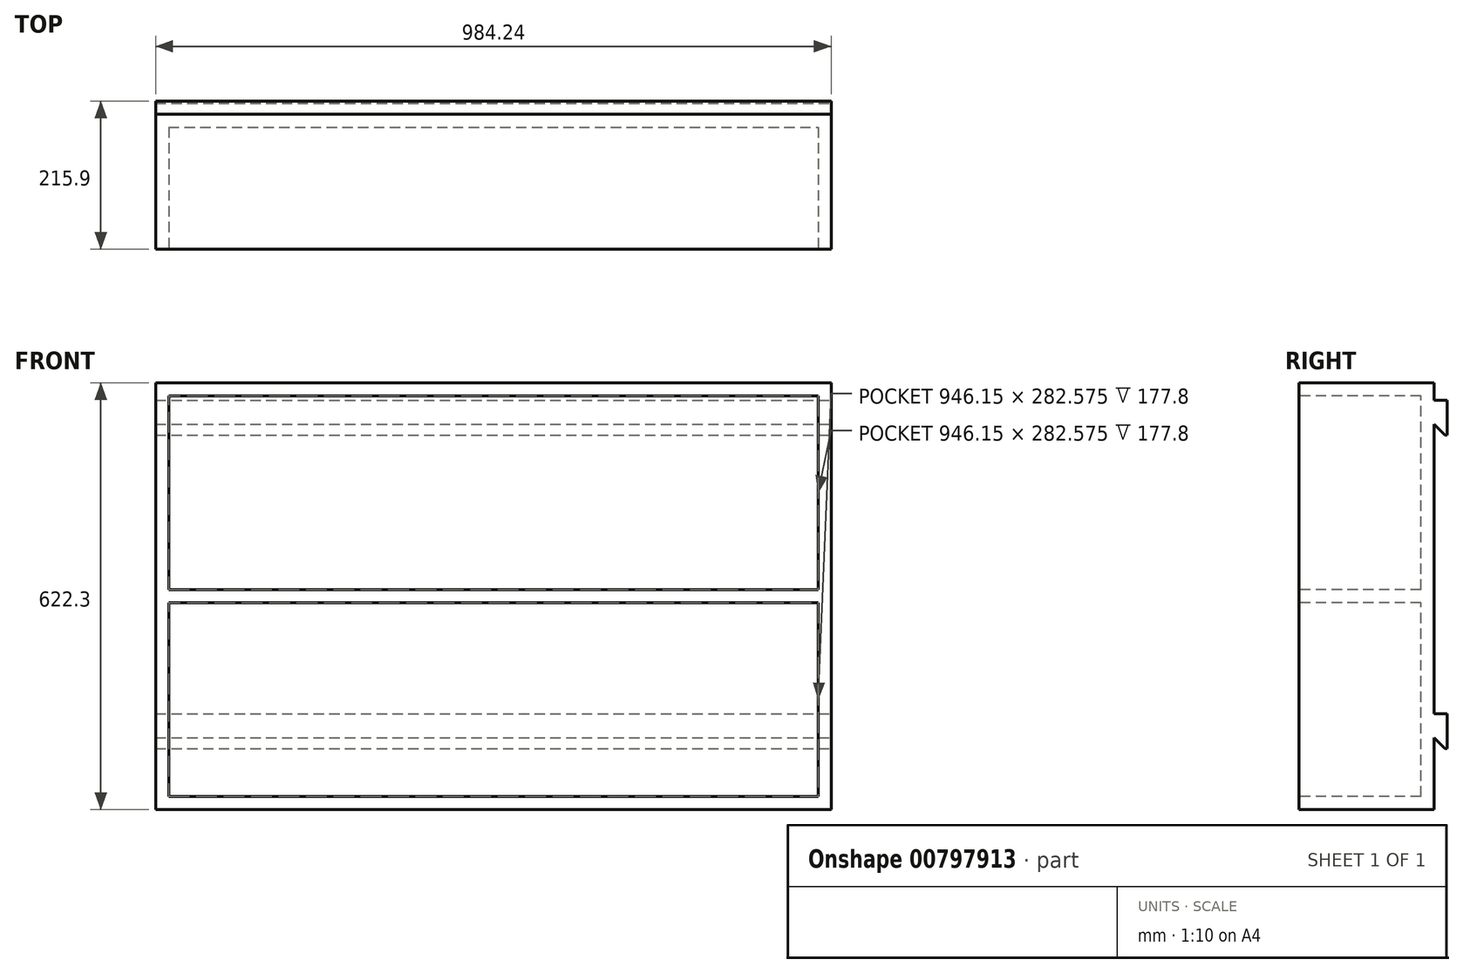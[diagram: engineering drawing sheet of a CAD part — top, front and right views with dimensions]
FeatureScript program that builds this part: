
annotation { "Feature Type Name" : "Feature", "Feature Type Description" : "" }
export const myFeature = defineFeature(function(context is Context, id is Id, definition is map)
    precondition{}
    {
        {
            var Q0;
            Q0=qCreatedBy(makeId("Front.planeOp"),FACE);
            var sketch = newSketch(context, id + "F0", { "sketchPlane" : qUnion([Q0])});
            skLineSegment(sketch, "E0.bottom", {"start": v(-492.12, -311.15) * mm, "end": v(492.13, -311.15) * mm});
            skLineSegment(sketch, "E0.top", {"start": v(-492.13, 311.15) * mm, "end": v(492.12, 311.15) * mm});
            skLineSegment(sketch, "E0.left", {"start": v(-492.12, -311.15) * mm, "end": v(-492.13, 311.15) * mm});
            skLineSegment(sketch, "E0.right", {"start": v(492.13, -311.15) * mm, "end": v(492.12, 311.15) * mm});
            skPoint(sketch, "E0.middle", {"position": v(0, 0) * mm});
            skLineSegment(sketch, "E1.0", {"start": v(-473.07, -292.1) * mm, "end": v(-473.08, 292.1) * mm});
            skLineSegment(sketch, "E1.1", {"start": v(-473.07, -292.1) * mm, "end": v(473.08, -292.1) * mm});
            skLineSegment(sketch, "E1.2", {"start": v(473.08, -292.1) * mm, "end": v(473.07, 292.1) * mm});
            skLineSegment(sketch, "E1.3", {"start": v(-473.08, 292.1) * mm, "end": v(473.07, 292.1) * mm});
            skLineSegment(sketch, "E2.0", {"start": v(-473.07, -9.53) * mm, "end": v(473.07, -9.53) * mm});
            skLineSegment(sketch, "E3.0", {"start": v(-473.07, 9.52) * mm, "end": v(473.07, 9.52) * mm});
            skSolve(sketch);
        }
        {
            var Q0;
            Q0=makeQuery(id+"F0.imprint","IMPRINT",FACE,{"disambiguationData":[TD([[makeQuery(id+"F0.imprint","IMPRINT",EDGE,{"derivedFrom":sQuery(id+"F0.wireOp",EDGE,"E0.bottom")}),1.0]])]});
            extrude(context, id + "F1", {"entities" : qUnion([Q0]), "oppositeDirection" : true, "depth" : 177.8 * mm, "offsetDistance" : 25.4 * mm});
        }
        {
            var Q0;
            Q0=makeQuery(id+"F1.opExtrude","CAP_FACE",FACE,{"disambiguationData":[OSD([sQuery(id+"F0.wireOp",EDGE,"E0.bottom"),sQuery(id+"F0.wireOp",EDGE,"E0.top"),sQuery(id+"F0.wireOp",EDGE,"E0.left"),sQuery(id+"F0.wireOp",EDGE,"E0.right"),sQuery(id+"F0.wireOp",EDGE,"E1.0"),sQuery(id+"F0.wireOp",EDGE,"E1.1"),sQuery(id+"F0.wireOp",EDGE,"E1.2"),sQuery(id+"F0.wireOp",EDGE,"E1.3")])],"isStart":false});
            var sketch = newSketch(context, id + "F2", { "sketchPlane" : qUnion([Q0])});
            skLineSegment(sketch, "E4.bottom", {"start": v(-492.12, 311.15) * mm, "end": v(492.12, 311.15) * mm});
            skLineSegment(sketch, "E4.top", {"start": v(-492.12, -311.15) * mm, "end": v(492.12, -311.15) * mm});
            skLineSegment(sketch, "E4.left", {"start": v(-492.12, 311.15) * mm, "end": v(-492.12, -311.15) * mm});
            skLineSegment(sketch, "E4.right", {"start": v(492.12, 311.15) * mm, "end": v(492.12, -311.15) * mm});
            skSolve(sketch);
        }
        {
            var Q0;
            Q0 = qSketchRegion(id + "F2", true);
            extrude(context, id + "F3", {"entities" : qUnion([Q0]), "operationType" : NewBodyOperationType.ADD, "depth" : 19.05 * mm, "offsetDistance" : 25.4 * mm});
        }
        {
            var Q0;
            {var subQ0=sQuery(id+"F0.wireOp",EDGE,"E2.0");Q0=makeQuery(id+"F0.imprint","IMPRINT",FACE,{"disambiguationData":[TD([[makeQuery(id+"F0.imprint","IMPRINT",EDGE,{"derivedFrom":subQ0}),1.0]])]});}
            extrude(context, id + "F4", {"entities" : qUnion([Q0]), "operationType" : NewBodyOperationType.ADD, "oppositeDirection" : true, "depth" : 177.8 * mm, "offsetDistance" : 25.4 * mm});
        }
        {
            var Q0;
            Q0=makeQuery(id+"F3.boolean.opBoolean","MERGE",FACE,{"derivedFrom":[makeQuery(id+"F1.opExtrude","SWEPT_FACE",FACE,{"disambiguationData":[OSD([sQuery(id+"F0.wireOp",EDGE,"E0.right")])]}),makeQuery(id+"F3.opExtrude","SWEPT_FACE",FACE,{"disambiguationData":[OSD([sQuery(id+"F2.wireOp",EDGE,"E4.left")])]})]});
            var sketch = newSketch(context, id + "F5", { "sketchPlane" : qUnion([Q0])});
            skLineSegment(sketch, "E5", {"start": v(196.85, 285.75) * mm, "end": v(215.9, 285.75) * mm});
            skLineSegment(sketch, "E6", {"start": v(215.9, 285.75) * mm, "end": v(215.9, 234.95) * mm});
            skLineSegment(sketch, "E7", {"start": v(215.9, 234.95) * mm, "end": v(212.73, 234.95) * mm});
            skLineSegment(sketch, "E8", {"start": v(212.73, 234.95) * mm, "end": v(196.85, 250.82) * mm});
            skLineSegment(sketch, "E9", {"start": v(196.85, -171.45) * mm, "end": v(215.9, -171.45) * mm});
            skLineSegment(sketch, "E10", {"start": v(215.9, -171.45) * mm, "end": v(215.9, -222.25) * mm});
            skLineSegment(sketch, "E11", {"start": v(215.9, -222.25) * mm, "end": v(212.73, -222.25) * mm});
            skLineSegment(sketch, "E12", {"start": v(212.73, -222.25) * mm, "end": v(196.85, -206.38) * mm});
            skSolve(sketch);
        }
        {
            var Q0;
            {var subQ1=sQuery(id+"F5.wireOp",EDGE,"E5");Q0=makeQuery(id+"F5.imprint","IMPRINT",FACE,{"disambiguationData":[TD([[makeQuery(id+"F5.imprint","IMPRINT",EDGE,{"derivedFrom":subQ1}),-1.0]])]});}
            var Q1;
            {var subQ1=sQuery(id+"F5.wireOp",EDGE,"E9");Q1=makeQuery(id+"F5.imprint","IMPRINT",FACE,{"disambiguationData":[TD([[makeQuery(id+"F5.imprint","IMPRINT",EDGE,{"derivedFrom":subQ1}),-1.0]])]});}
            extrude(context, id + "F6", {"entities" : qUnion([Q0, Q1]), "operationType" : NewBodyOperationType.ADD, "oppositeDirection" : true, "depth" : 984.25 * mm, "offsetDistance" : 25.4 * mm});
        }
    });
